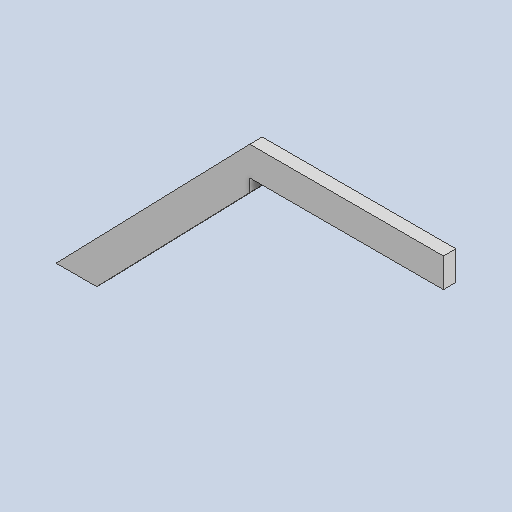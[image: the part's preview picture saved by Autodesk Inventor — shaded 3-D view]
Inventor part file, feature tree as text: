
AUTODESK INVENTOR PART (.ipt)
format: ipt  version: 2025 (Build 290162000, 162)  size: 141,312 bytes
history: native  units: in
note: dims shown in document units (in); Inventor stores cm internally (conversion verified against a paired STEP export)
features: other x5, reference x3, extrude x1, sketch x1
ambient origin geometry x8: Origin, YZ Plane, XZ Plane, XY Plane, X Axis, Y Axis, Z Axis, Center Point
bodies: Solid1 (feature_tree)
feature tree (10):
  extrude  "Extrusion1"  Depth=3.5in
  sketch  "Sketch1"  dims[d0=3.5in d1=3.5in d2=1.5in d3=0.0in]
  reference  "Reference1"
  reference  "Reference2"
  reference  "Reference3"
  other  "<userpath>\Documents\Tburn24\F_Legs2\F_Legs2.iam"
  other  "F_Legs2.iam"
  other  "8'x2x4:4"
  other  "back_side:1"
  other  "side-side:2"
